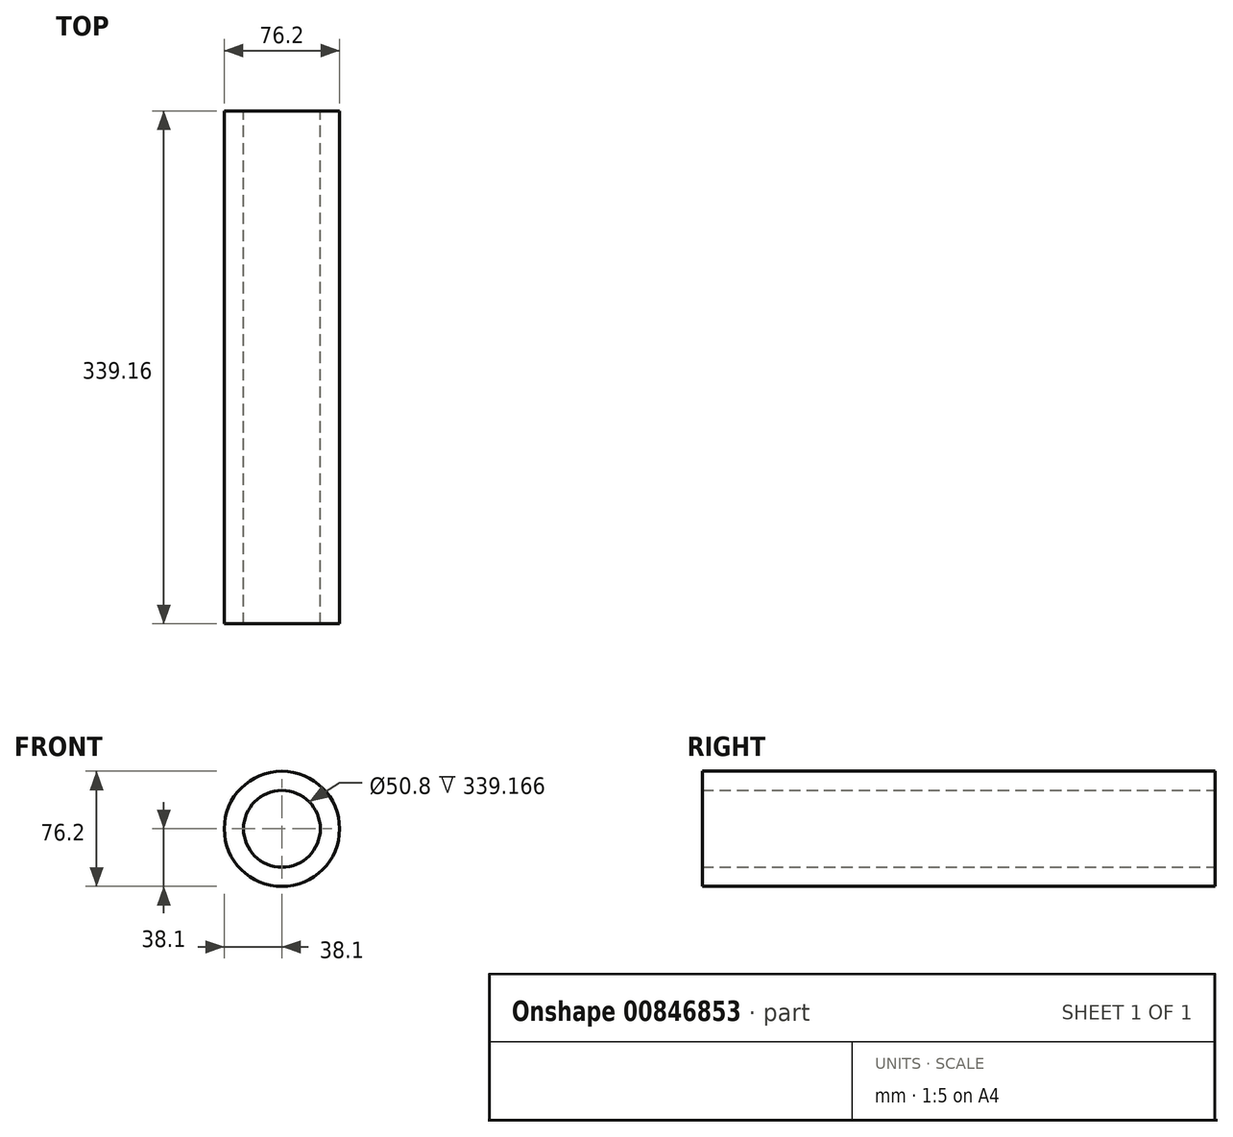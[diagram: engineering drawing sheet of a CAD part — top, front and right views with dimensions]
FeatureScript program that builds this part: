
annotation { "Feature Type Name" : "Feature", "Feature Type Description" : "" }
export const myFeature = defineFeature(function(context is Context, id is Id, definition is map)
    precondition{}
    {
        {
            var Q0;
            Q0=qCreatedBy(makeId("Front.planeOp"),FACE);
            var sketch = newSketch(context, id + "F0", { "sketchPlane" : qUnion([Q0])});
            skCircle(sketch, "E0", {"center": v(0, 0) * mm, "radius": 38.1 * mm});
            skCircle(sketch, "E1", {"center": v(0, 0) * mm, "radius": 25.4 * mm});
            skSolve(sketch);
        }
        {
            var Q0;
            Q0 = qSketchRegion(id + "F0", true);
            extrude(context, id + "F1", {"entities" : qUnion([Q0]), "depth" : 339.17 * mm, "offsetDistance" : 25.4 * mm, "symmetric" : true});
        }
    });
